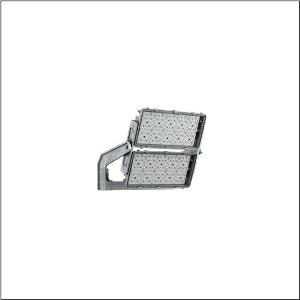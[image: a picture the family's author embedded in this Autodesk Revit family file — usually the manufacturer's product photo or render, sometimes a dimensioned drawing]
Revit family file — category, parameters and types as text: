
# Revit family: floodlight_fl_11_maxi_remote___rs07_5xa779514k01aa_47cf
name_source: partatom
category: Lighting Fixtures
units: mm (PartAtom-declared; Revit-internal decimal feet)

## family parameters
Cut with Voids When Loaded = No
Host = Face
Light Source = No
Part Type = Normal
Room Calculation Point = No
Round Connector Dimension = Use Diameter
Shared = No

## types (1)
- --- (1 x LED, 88570 lm, 916.8 W, 5700K)
    Apparent Load = 917 VA
    CIE Flux Codes = 80 93 99 100 99
    Color Rendering = 90
    Color Temperature = 5700K
    Default Elevation = 1800 mm
    Description = Floodlight FL 11  maxi  Remote floodlight; light control with lens of PMMA; cover panel of toughened safety glass, transparent; light distribution: RS07, rotationally symmetric direct distribution, LEDcolour temperature: 5700K, rated luminous flux: 88.570lm, colour rendering: CRI > 90, light colour: 957; luminous efficacy: 97lm/W; brightness control: DMX+RDM; with terminal, 6-pole, max. 2.5mm², mains connection: 220..240V/380..400V AC, 50/60Hz, surge voltage resistance: line to ground: 10kV, ECG replaceable separately, no afterglow with DALI off / DMX off command, LED unit replaceable without ESD environment, dustproof LED module, dimming range 10..100%; 917W floodlight with 2x LED unit of diecast aluminium, coated grey; length: 713mm / width: 651mm / height: 338mm; mounting bracket, of diecast aluminium, uncoated, natural, equipment: Power, protection rating (complete): IP66; insulation class (complete): insulation class I (protective earthing); certification: CE, ENEC, VDE; ball protection: ball impact resistance with accessories, impact resistance: IK07; rated ambient temperature 10°C, only for outdoor installations, permissible operating ambient temperature: -40..+30°C, permissible storage temperature: -40..+85°C; packaging unit: 1 piece

Light Distribution: RS07
    Height = 320 mm
    Lamp = 1 x LED
    Lamp Light Flux = 88570 lm
    Lamp Power = 916.8 W
    Lamp count = 1
    Length = 712 mm
    Luminous efficacy = 97 lm/W
    Manufacturer = Siteco
    ModVariant = No
    Model = 5XA779514K01AA
    Mounting Place = Ceiling
    Mounting Type = Surface mounted
    Number of Poles = 1
    OnlyDefault = Yes
    Power Factor = 1
    Product Name = Floodlight FL 11 maxi Remote | RS07
    Product group = floodlight | ceiling mounted
    ProductGroupID = 302
    Protection Class = Protection class I
    Protection Degree = IP 66
    RLX_Detail_Level = 1
    RLX_Emergency_Light_Flux = 0 lm
    RLX_Emergency_Type = 0
    RLX_Emergency_Type_DB = No
    RlxData = <blob elided: 41221 chars, md5=e50836ae>
    Socket = socket
    Standby Power = 0 W
    System Light Flux = 88570 lm
    System Power = 917 W
    Type Comments = factory setting: luminous flux: 100 % | dim-lin: 254 | 950 mA
    Type Image = l_1006788.jpg
    URL = http://relux.com
    VarID = @adj_114565
    Voltage = 0 V
    Weight = 0.00 kg
    Width = 655 mm

## geometry (parser evidence)
native form markers: Blend x4, Sweep x12
no freeform markers — native parametric forms only
